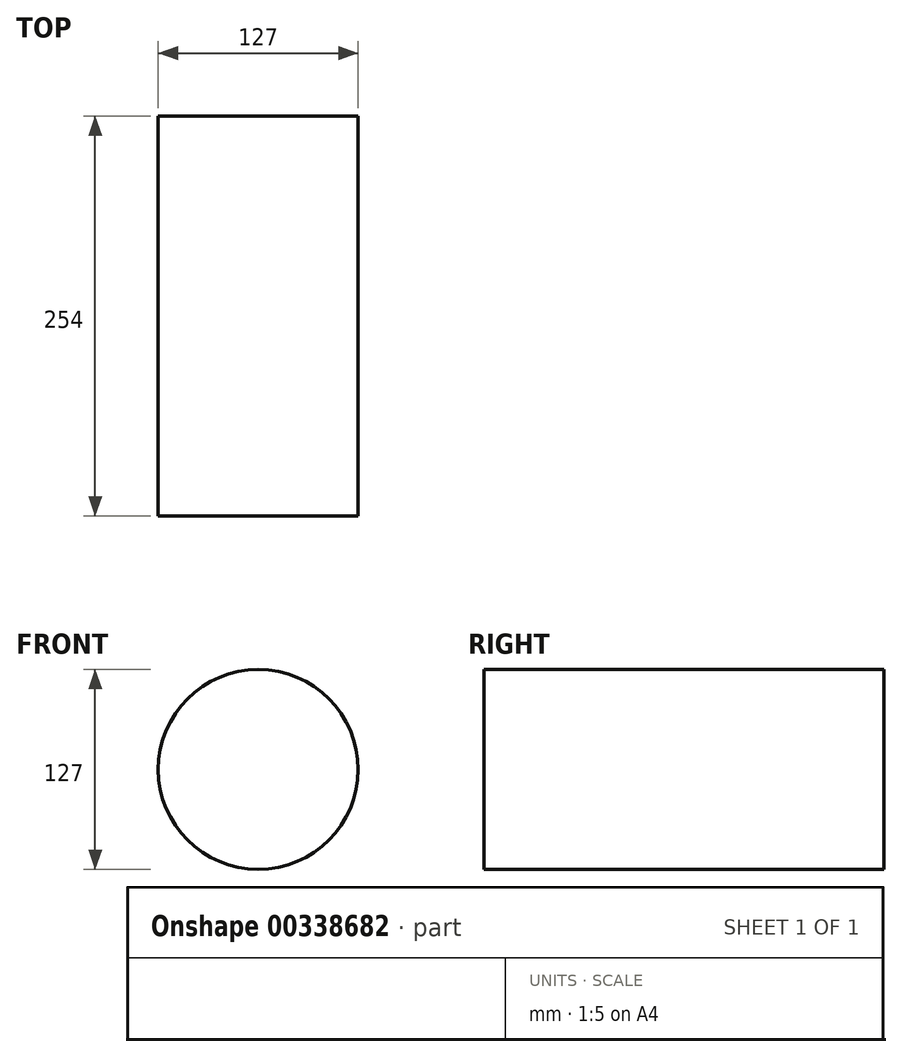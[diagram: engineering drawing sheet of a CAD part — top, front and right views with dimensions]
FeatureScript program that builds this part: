
annotation { "Feature Type Name" : "Feature", "Feature Type Description" : "" }
export const myFeature = defineFeature(function(context is Context, id is Id, definition is map)
    precondition{}
    {
        {
            var Q0;
            Q0=qCreatedBy(makeId("Front.planeOp"),FACE);
            var sketch = newSketch(context, id + "F0", { "sketchPlane" : qUnion([Q0])});
            skCircle(sketch, "E0", {"center": v(0, 0) * mm, "radius": 63.5 * mm});
            skSolve(sketch);
        }
        {
            var Q0;
            Q0 = qSketchRegion(id + "F0", true);
            extrude(context, id + "F1", {"entities" : qUnion([Q0]), "endBound" : BoundingType.SYMMETRIC, "depth" : 254 * mm});
        }
    });
